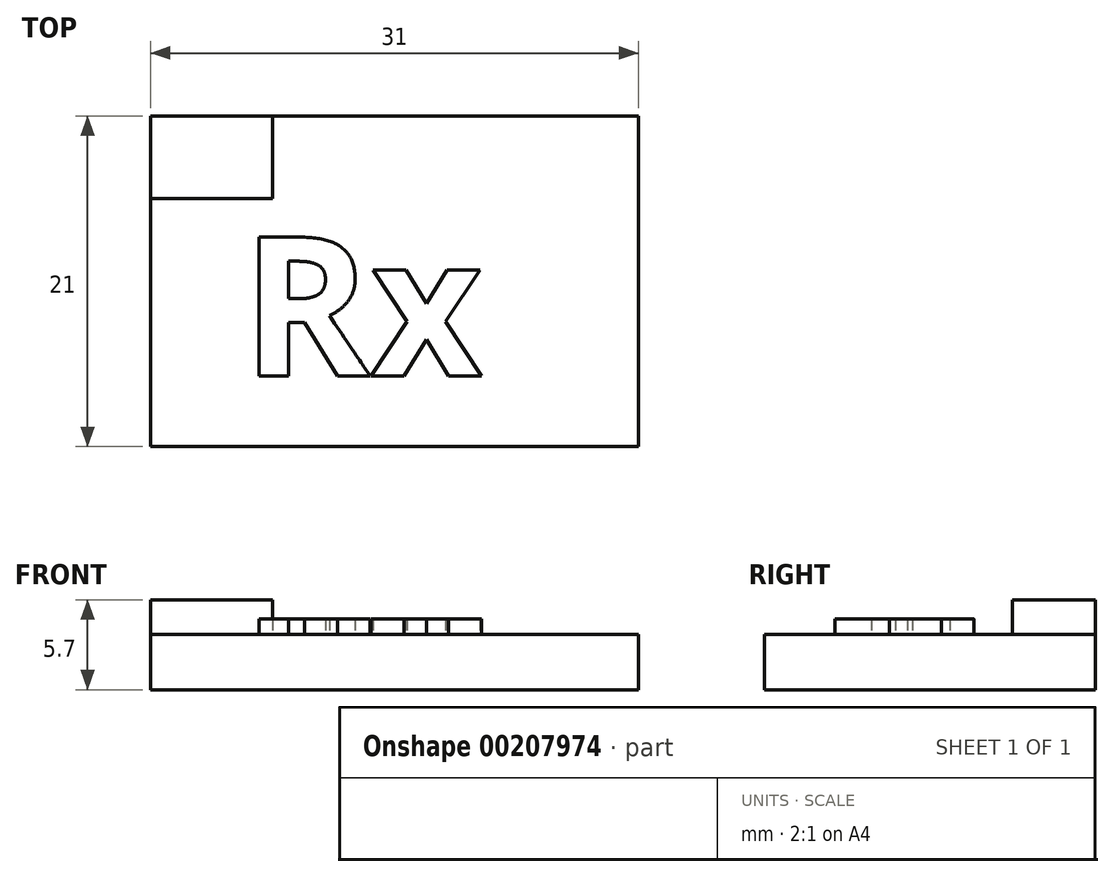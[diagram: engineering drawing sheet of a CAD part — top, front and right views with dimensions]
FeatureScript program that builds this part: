
annotation { "Feature Type Name" : "Feature", "Feature Type Description" : "" }
export const myFeature = defineFeature(function(context is Context, id is Id, definition is map)
    precondition{}
    {
        {
            var Q0;
            Q0=qCreatedBy(makeId("Top.planeOp"),FACE);
            var sketch = newSketch(context, id + "F0", { "sketchPlane" : qUnion([Q0])});
            skLineSegment(sketch, "E0.bottom", {"start": v(28.56, 0) * mm, "end": v(-2.44, 0) * mm});
            skLineSegment(sketch, "E0.top", {"start": v(28.56, 21) * mm, "end": v(-2.44, 21) * mm});
            skLineSegment(sketch, "E0.left", {"start": v(28.56, 0) * mm, "end": v(28.56, 21) * mm});
            skLineSegment(sketch, "E0.right", {"start": v(-2.44, 0) * mm, "end": v(-2.44, 21) * mm});
            skSolve(sketch);
        }
        {
            var Q0;
            Q0=makeQuery(id+"F0.imprint","IMPRINT",FACE,{"disambiguationData":[TD([[makeQuery(id+"F0.imprint","IMPRINT",EDGE,{"derivedFrom":sQuery(id+"F0.wireOp",EDGE,"E0.bottom")}),-1.0]])]});
            extrude(context, id + "F1", {"entities" : qUnion([Q0]), "depth" : 3.5 * mm});
        }
        {
            var Q0;
            Q0=makeQuery(id+"F1.opExtrude","CAP_FACE",FACE,{"disambiguationData":[OSD([sQuery(id+"F0.wireOp",EDGE,"E0.bottom"),sQuery(id+"F0.wireOp",EDGE,"E0.top"),sQuery(id+"F0.wireOp",EDGE,"E0.left"),sQuery(id+"F0.wireOp",EDGE,"E0.right")])],"isStart":false});
            var sketch = newSketch(context, id + "F2", { "sketchPlane" : qUnion([Q0])});
            skLineSegment(sketch, "E1.bottom", {"start": v(-2.44, 21) * mm, "end": v(5.3, 21) * mm});
            skLineSegment(sketch, "E1.top", {"start": v(-2.44, 15.75) * mm, "end": v(5.3, 15.75) * mm});
            skLineSegment(sketch, "E1.left", {"start": v(-2.44, 21) * mm, "end": v(-2.44, 15.75) * mm});
            skLineSegment(sketch, "E1.right", {"start": v(5.3, 21) * mm, "end": v(5.3, 15.75) * mm});
            skSolve(sketch);
        }
        {
            var Q0;
            Q0=makeQuery(id+"F2.imprint","IMPRINT",FACE,{"disambiguationData":[TD([[makeQuery(id+"F2.imprint","IMPRINT",EDGE,{"derivedFrom":sQuery(id+"F2.wireOp",EDGE,"E1.bottom")}),1.0]])]});
            extrude(context, id + "F3", {"entities" : qUnion([Q0]), "operationType" : NewBodyOperationType.ADD, "depth" : 2.2 * mm});
        }
        {
            var Q0;
            Q0=makeQuery(id+"F1.opExtrude","CAP_FACE",FACE,{"disambiguationData":[OSD([sQuery(id+"F0.wireOp",EDGE,"E0.bottom"),sQuery(id+"F0.wireOp",EDGE,"E0.top"),sQuery(id+"F0.wireOp",EDGE,"E0.left"),sQuery(id+"F0.wireOp",EDGE,"E0.right")])],"isStart":false});
            var sketch = newSketch(context, id + "F4", { "sketchPlane" : qUnion([Q0])});
            skText(sketch, "E2", { "text": "Rx", "fontName": "OpenSans-Bold.ttf"});
            const initialGuessF4  = {"E2": [0.00336, 0.00448, 1, 0, 0.00889]};
            skSetInitialGuess(sketch, initialGuessF4);
            skSolve(sketch);
        }
        {
            var Q0;
            Q0=makeQuery(id+"F4.imprint","IMPRINT",FACE,{"disambiguationData":[TD([[makeQuery(id+"F4.imprint","IMPRINT",EDGE,{"derivedFrom":sQuery(id+"F4.wireOp",EDGE,"E2.sketch_text.stroke-0")}),-1.0]])]});
            var Q1;
            Q1=makeQuery(id+"F4.imprint","IMPRINT",FACE,{"disambiguationData":[TD([[makeQuery(id+"F4.imprint","IMPRINT",EDGE,{"derivedFrom":sQuery(id+"F4.wireOp",EDGE,"E2.sketch_text.stroke-19")}),-1.0]])]});
            extrude(context, id + "F5", {"entities" : qUnion([Q0, Q1]), "operationType" : NewBodyOperationType.ADD, "depth" : 1 * mm});
        }
    });
